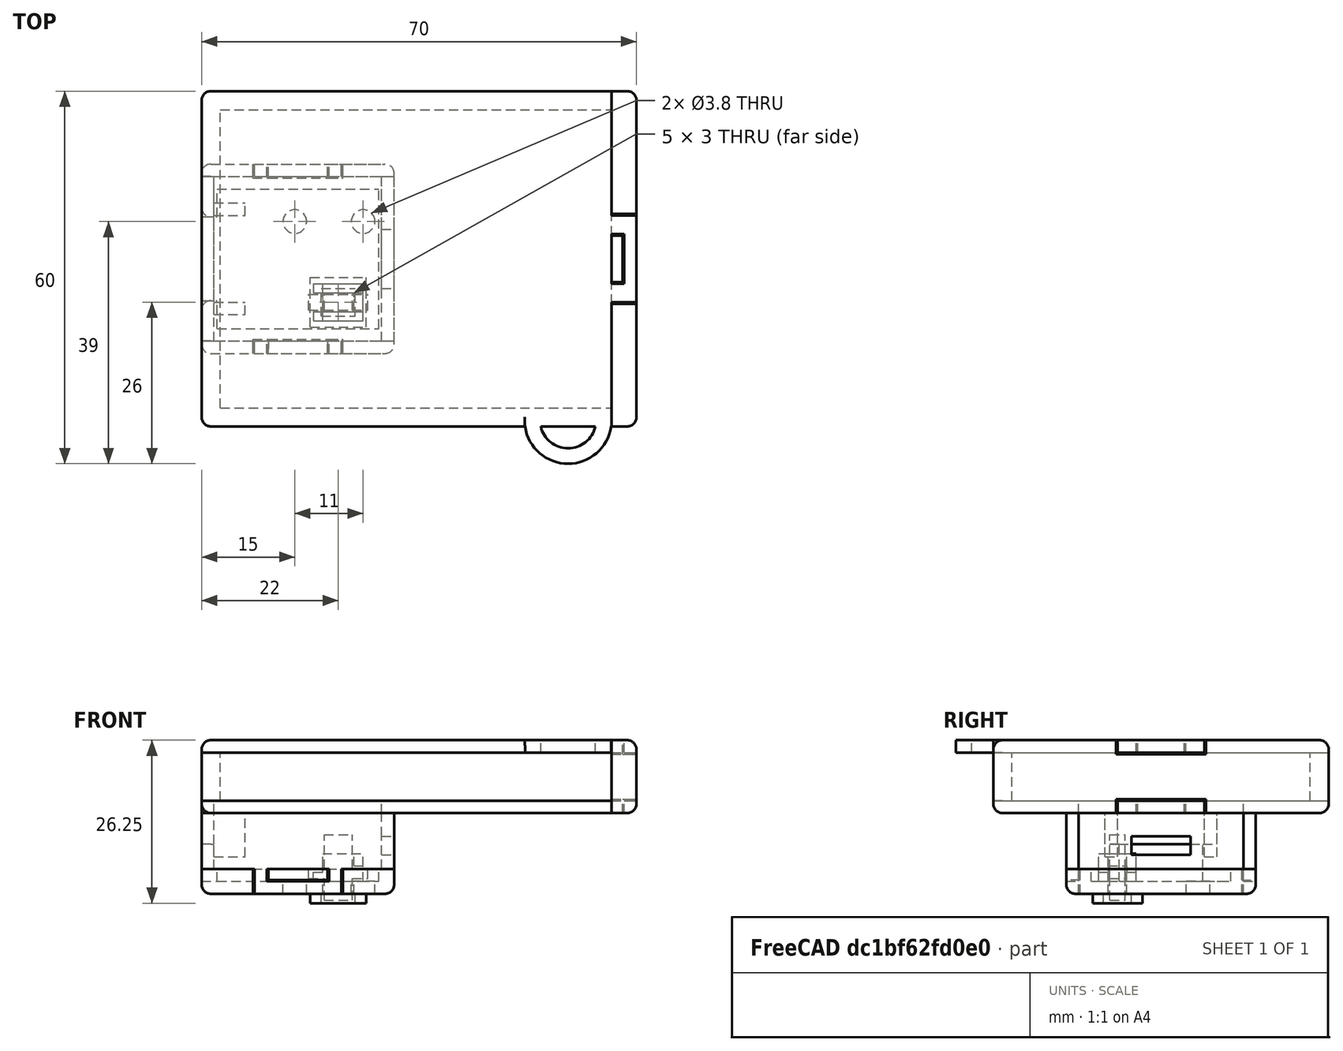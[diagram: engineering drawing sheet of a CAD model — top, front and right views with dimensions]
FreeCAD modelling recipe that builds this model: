
FCSTD DOCUMENT  (FreeCAD 0.18R16131 (Git))
Label: New_USB_Charger_Rev_1
License: All rights reserved
LicenseURL: http://en.wikipedia.org/wiki/All_rights_reserved
objects: Part::Box×62, Part::Cut×21, Part::MultiFuse×11, Part::Fillet×7, Part::Cylinder×4
note: 105 computed .brp shape members not serialized (recipe doc carries the construction recipe); baked Part::Feature solids carry a one-line shape summary decoded from their .brp

FEATURE [Part::Box] Box  label="Cube"
  AttacherType = Attacher::AttachEngine3D
  Height = 7.75
  Length = 3
  Placement = pos=(-1,-3,0) rot=(0,0,1;0rad)
  Width = 54
FEATURE [Part::Box] Box003  label="Cube003"
  AttacherType = Attacher::AttachEngine3D
  Height = 7.75
  Length = 63
  Placement = pos=(2,-3,0) rot=(0,0,1;0rad)
  Width = 3
FEATURE [Part::Box] Box004  label="Cube004"
  AttacherType = Attacher::AttachEngine3D
  Height = 7.75
  Length = 63
  Placement = pos=(2,48,0) rot=(0,0,1;0rad)
  Width = 3
FEATURE [Part::Box] Box023  label="Cube023"
  AttacherType = Attacher::AttachEngine3D
  Height = 2
  Length = 66
  Placement = pos=(-1,-3,7.75) rot=(0,0,1;0rad)
  Width = 54
FEATURE [Part::Box] Box024  label="Cube024"
  AttacherType = Attacher::AttachEngine3D
  Height = 11.75
  Length = 4
  Placement = pos=(65,-3,-2) rot=(0,0,1;0rad)
  Width = 54
FEATURE [Part::Box] Box029  label="Cube029"
  AttacherType = Attacher::AttachEngine3D
  Height = 5
  Length = 2
  Placement = pos=(-1,10.75,-7) rot=(0,0,1;0rad)
  Width = 26.5
FEATURE [Part::Box] Box031  label="Cube031"
  AttacherType = Attacher::AttachEngine3D
  Height = 4
  Length = 2
  Placement = pos=(-1,10.75,-11) rot=(0,0,1;0rad)
  Width = 6.5
FEATURE [Part::Box] Box032  label="Cube032"
  AttacherType = Attacher::AttachEngine3D
  Height = 4
  Length = 2
  Placement = pos=(-1,30.75,-11) rot=(0,0,1;0rad)
  Width = 6.5
FEATURE [Part::Box] Box033  label="Cube033"
  AttacherType = Attacher::AttachEngine3D
  Height = 3.7
  Length = 2
  Placement = pos=(28,10.75,-5.7) rot=(0,0,1;0rad)
  Width = 26.5
FEATURE [Part::Box] Box034  label="Cube034"
  AttacherType = Attacher::AttachEngine3D
  Height = 3
  Length = 2
  Placement = pos=(28,28.75,-8.7) rot=(0,0,1;0rad)
  Width = 8.5
FEATURE [Part::Box] Box035  label="Cube035"
  AttacherType = Attacher::AttachEngine3D
  Height = 3
  Length = 2
  Placement = pos=(28,10.75,-8.7) rot=(0,0,1;0rad)
  Width = 8.5
FEATURE [Part::Box] Box038  label="Cube038"
  AttacherType = Attacher::AttachEngine3D
  Height = 2.3
  Length = 2
  Placement = pos=(28,10.75,-11) rot=(0,0,1;0rad)
  Width = 26.5
FEATURE [Part::Box] Box039  label="Cube039"
  AttacherType = Attacher::AttachEngine3D
  Height = 7
  Length = 5
  Placement = pos=(1,15,-9) rot=(0,0,1;0rad)
  Width = 2
FEATURE [Part::Box] Box040  label="Cube040"
  AttacherType = Attacher::AttachEngine3D
  Height = 7
  Length = 5
  Placement = pos=(1,31,-9) rot=(0,0,1;0rad)
  Width = 2
FEATURE [Part::Box] Box041  label="Cube041"
  AttacherType = Attacher::AttachEngine3D
  Height = 2
  Length = 66
  Placement = pos=(-1,-3,-2) rot=(0,0,1;0rad)
  Width = 54
FEATURE [Part::Box] Box042  label="Cube042"
  AttacherType = Attacher::AttachEngine3D
  Height = 2
  Length = 27
  Placement = pos=(1,10.75,-2) rot=(0,0,1;0rad)
  Width = 26.5
FEATURE [Part::Box] Box043  label="Cube043"
  AttacherType = Attacher::AttachEngine3D
  Height = 2
  Length = 4
  Placement = pos=(65,17,-2) rot=(0,0,1;0rad)
  Width = 3
FEATURE [Part::Box] Box044  label="Cube044"
  AttacherType = Attacher::AttachEngine3D
  Height = 2
  Length = 4
  Placement = pos=(65,28,-2) rot=(0,0,1;0rad)
  Width = 3
FEATURE [Part::Box] Box045  label="Cube045"
  AttacherType = Attacher::AttachEngine3D
  Height = 2
  Length = 2
  Placement = pos=(67,20,-2) rot=(0,0,1;0rad)
  Width = 8
FEATURE [Part::MultiFuse] Fusion001
  Shapes = -> [Box041,Box044,Box045,Box043]
FEATURE [Part::MultiFuse] Fusion
  Shapes = -> [Box,Box003,Box004]
FEATURE [Part::Fillet] Fillet  label="Main_Sides"
  Base = -> Fusion
  Edges = 2 edges r=1.5: [Edge21,Edge28]
FEATURE [Part::Box] Box048  label="Cube048"
  AttacherType = Attacher::AttachEngine3D
  Height = 2
  Length = 4
  Placement = pos=(65,17,7.75) rot=(0,0,1;0rad)
  Width = 3
FEATURE [Part::Box] Box049  label="Cube049"
  AttacherType = Attacher::AttachEngine3D
  Height = 2
  Length = 4
  Placement = pos=(65,28,7.75) rot=(0,0,1;0rad)
  Width = 3
FEATURE [Part::Box] Box050  label="Cube050"
  AttacherType = Attacher::AttachEngine3D
  Height = 2
  Length = 2
  Placement = pos=(67,20,7.75) rot=(0,0,1;0rad)
  Width = 8
FEATURE [Part::Cylinder] Cylinder005
  Angle = 360
  AttacherType = Attacher::AttachEngine3D
  Height = 2
  Placement = pos=(58,-2,7.75) rot=(0,0,1;0rad)
  Radius = 7
FEATURE [Part::Cylinder] Cylinder006
  Angle = 360
  AttacherType = Attacher::AttachEngine3D
  Height = 2
  Placement = pos=(58,-2,7.75) rot=(0,0,1;0rad)
  Radius = 4.5
FEATURE [Part::Box] Box051  label="Cube051"
  AttacherType = Attacher::AttachEngine3D
  Height = 2
  Length = 14
  Placement = pos=(51,-3,7.75) rot=(0,0,1;0rad)
  Width = 8
FEATURE [Part::Fillet] Fillet011
  Base = -> Box024
  Edges = 8 edges r=1.5: [Edge5,Edge6,Edge7,Edge8,Edge9,Edge10,Edge11,Edge12]
FEATURE [Part::Box] Box052  label="Cube052"
  AttacherType = Attacher::AttachEngine3D
  Height = 2.25
  Length = 4
  Placement = pos=(65,16.75,7.5) rot=(0,0,1;0rad)
  Width = 3.5
FEATURE [Part::Box] Box053  label="Cube053"
  AttacherType = Attacher::AttachEngine3D
  Height = 2.25
  Length = 4
  Placement = pos=(65,27.75,7.5) rot=(0,0,1;0rad)
  Width = 3.5
FEATURE [Part::Box] Box054  label="Cube054"
  AttacherType = Attacher::AttachEngine3D
  Height = 2.25
  Length = 2.25
  Placement = pos=(66.75,20.25,7.5) rot=(0,0,1;0rad)
  Width = 7.5
FEATURE [Part::Box] Box055  label="Cube055"
  AttacherType = Attacher::AttachEngine3D
  Height = 2.25
  Length = 4
  Placement = pos=(65,16.75,-2) rot=(0,0,1;0rad)
  Width = 3.5
FEATURE [Part::Box] Box056  label="Cube056"
  AttacherType = Attacher::AttachEngine3D
  Height = 2.25
  Length = 2.25
  Placement = pos=(66.75,20.25,-2) rot=(0,0,1;0rad)
  Width = 7.5
FEATURE [Part::Box] Box057  label="Cube057"
  AttacherType = Attacher::AttachEngine3D
  Height = 2.25
  Length = 4
  Placement = pos=(65,27.75,-2) rot=(0,0,1;0rad)
  Width = 3.5
FEATURE [Part::Cut] Cut007
  Base = -> Fillet011
  Tool = -> Box057
FEATURE [Part::Cut] Cut008
  Base = -> Cut007
  Tool = -> Box055
FEATURE [Part::Cut] Cut009
  Base = -> Cut008
  Tool = -> Box056
FEATURE [Part::Cut] Cut010
  Base = -> Cut009
  Tool = -> Box053
FEATURE [Part::Cut] Cut011
  Base = -> Cut010
  Tool = -> Box052
FEATURE [Part::Cut] Cut012  label="Battery_Cover"
  Base = -> Cut011
  Tool = -> Box054
FEATURE [Part::Cut] Cut
  Base = -> Fusion001
  Tool = -> Box042
FEATURE [Part::Box] Box058  label="Cube058"
  AttacherType = Attacher::AttachEngine3D
  Height = 2
  Length = 31
  Placement = pos=(-1,8.75,-15) rot=(0,0,1;0rad)
  Width = 30.5
FEATURE [Part::Cylinder] Cylinder007
  Angle = 360
  AttacherType = Attacher::AttachEngine3D
  Height = 2
  Placement = pos=(14,30,-15) rot=(0,0,1;0rad)
  Radius = 1.9
FEATURE [Part::Cylinder] Cylinder008
  Angle = 360
  AttacherType = Attacher::AttachEngine3D
  Height = 2
  Placement = pos=(25,30,-15) rot=(0,0,1;0rad)
  Radius = 1.9
FEATURE [Part::Cut] Cut016
  Base = -> Cylinder005
  Tool = -> Cylinder006
FEATURE [Part::Cut] Cut017
  Base = -> Cut016
  Tool = -> Box051
FEATURE [Part::MultiFuse] Fusion007
  Shapes = -> [Cut017,Box023,Box048,Box050,Box049]
FEATURE [Part::Fillet] Fillet015  label="Main_Bottom"
  Base = -> Fusion007
  Edges = 8 edges r=1.5: [Edge23,Edge28,Edge29,Edge30,Edge32,Edge34,Edge55,Edge65]
FEATURE [Part::Box] Box067  label="Cube067"
  AttacherType = Attacher::AttachEngine3D
  Height = 10.5
  Length = 4.5
  Placement = pos=(18.75,15.75,-16) rot=(0,0,1;0rad)
  Width = 2.5
FEATURE [Part::Box] Box068  label="Cube068"
  AttacherType = Attacher::AttachEngine3D
  Height = 2
  Length = 5
  Placement = pos=(18.5,15.5,-15) rot=(0,0,1;0rad)
  Width = 3
FEATURE [Part::Box] Box069  label="Cube069"
  AttacherType = Attacher::AttachEngine3D
  Height = 2
  Length = 8
  Placement = pos=(17,14,-10.5) rot=(0,0,1;0rad)
  Width = 6
FEATURE [Part::Box] Box070  label="Cube070"
  AttacherType = Attacher::AttachEngine3D
  Height = 2
  Length = 5
  Placement = pos=(18.5,15.5,-10.5) rot=(0,0,1;0rad)
  Width = 3
FEATURE [Part::Box] Box071  label="Cube071"
  AttacherType = Attacher::AttachEngine3D
  Height = 9
  Length = 31
  Placement = pos=(-1,37.25,-11) rot=(0,0,1;0rad)
  Width = 2
FEATURE [Part::Box] Box072  label="Cube072"
  AttacherType = Attacher::AttachEngine3D
  Height = 4
  Length = 2
  Placement = pos=(7.5,37.25,-15) rot=(0,0,1;0rad)
  Width = 2
FEATURE [Part::Box] Box073  label="Cube073"
  AttacherType = Attacher::AttachEngine3D
  Height = 4
  Length = 2
  Placement = pos=(19.5,37.25,-15) rot=(0,0,1;0rad)
  Width = 2
FEATURE [Part::Box] Box074  label="Cube074"
  AttacherType = Attacher::AttachEngine3D
  Height = 2
  Length = 10
  Placement = pos=(9.5,37.25,-15) rot=(0,0,1;0rad)
  Width = 2
FEATURE [Part::Box] Box075  label="Cube075"
  AttacherType = Attacher::AttachEngine3D
  Height = 9
  Length = 31
  Placement = pos=(-1,8.75,-11) rot=(0,0,1;0rad)
  Width = 2
FEATURE [Part::Box] Box076  label="Cube076"
  AttacherType = Attacher::AttachEngine3D
  Height = 4
  Length = 2
  Placement = pos=(7.5,8.75,-15) rot=(0,0,1;0rad)
  Width = 2
FEATURE [Part::Box] Box077  label="Cube077"
  AttacherType = Attacher::AttachEngine3D
  Height = 4
  Length = 2
  Placement = pos=(19.5,8.75,-15) rot=(0,0,1;0rad)
  Width = 2
FEATURE [Part::Box] Box078  label="Cube078"
  AttacherType = Attacher::AttachEngine3D
  Height = 2
  Length = 10
  Placement = pos=(9.5,8.75,-15) rot=(0,0,1;0rad)
  Width = 2
FEATURE [Part::Box] Box079  label="Cube079"
  AttacherType = Attacher::AttachEngine3D
  Height = 2
  Length = 31
  Placement = pos=(-1,8.75,-13) rot=(0,0,1;0rad)
  Width = 2
FEATURE [Part::Box] Box080  label="Cube080"
  AttacherType = Attacher::AttachEngine3D
  Height = 2
  Length = 26
  Placement = pos=(1.5,10.75,-13) rot=(0,0,1;0rad)
  Width = 2
FEATURE [Part::Box] Box081  label="Cube081"
  AttacherType = Attacher::AttachEngine3D
  Height = 2
  Length = 31
  Placement = pos=(-1,37.25,-13) rot=(0,0,1;0rad)
  Width = 2
FEATURE [Part::Box] Box082  label="Cube082"
  AttacherType = Attacher::AttachEngine3D
  Height = 2
  Length = 26
  Placement = pos=(1.5,35.25,-13) rot=(0,0,1;0rad)
  Width = 2
FEATURE [Part::MultiFuse] Fusion012
  Shapes = -> [Box080,Box079,Box081,Box082,Box058]
FEATURE [Part::Fillet] Fillet019
  Base = -> Fusion012
  Edges = 12 edges r=1.5: [Edge1,Edge2,Edge3,Edge4,Edge5,Edge7,Edge10,Edge12,Edge17,Edge32,Edge33,Edge35]
FEATURE [Part::Box] Box083  label="Cube083"
  AttacherType = Attacher::AttachEngine3D
  Height = 4
  Length = 2.5
  Placement = pos=(19.25,8.75,-15) rot=(0,0,1;0rad)
  Width = 2.25
FEATURE [Part::Box] Box084  label="Cube084"
  AttacherType = Attacher::AttachEngine3D
  Height = 4
  Length = 2.5
  Placement = pos=(7.25,8.75,-15) rot=(0,0,1;0rad)
  Width = 2.25
FEATURE [Part::Box] Box085  label="Cube085"
  AttacherType = Attacher::AttachEngine3D
  Height = 2.25
  Length = 10
  Placement = pos=(9.5,8.75,-15) rot=(0,0,1;0rad)
  Width = 2.25
FEATURE [Part::Box] Box086  label="Cube086"
  AttacherType = Attacher::AttachEngine3D
  Height = 4
  Length = 2.5
  Placement = pos=(7.25,37,-15) rot=(0,0,1;0rad)
  Width = 2.25
FEATURE [Part::Box] Box087  label="Cube087"
  AttacherType = Attacher::AttachEngine3D
  Height = 4
  Length = 2.5
  Placement = pos=(19.25,37,-15) rot=(0,0,1;0rad)
  Width = 2.25
FEATURE [Part::Box] Box088  label="Cube088"
  AttacherType = Attacher::AttachEngine3D
  Height = 2.25
  Length = 10
  Placement = pos=(9.5,37,-15) rot=(0,0,1;0rad)
  Width = 2.25
FEATURE [Part::MultiFuse] Fusion015
  Shapes = -> [Cut,Box029,Box031,Box032,Box033,Box034,Box035,Box038,Box039,Box040]
FEATURE [Part::Cut] Cut022
  Base = -> Fillet019
  Tool = -> Box084
FEATURE [Part::Cut] Cut023
  Base = -> Cut022
  Tool = -> Box083
FEATURE [Part::Cut] Cut024
  Base = -> Cut023
  Tool = -> Box085
FEATURE [Part::MultiFuse] Fusion016
  Shapes = -> [Box078,Box077,Box076,Box075]
FEATURE [Part::Fillet] Fillet023  label="Top_Side_1"
  Base = -> Fusion016
  Edges = 5 edges r=1.5: [Edge1,Edge9,Edge21,Edge28,Edge43]
FEATURE [Part::Cut] Cut025
  Base = -> Cut024
  Tool = -> Box088
FEATURE [Part::Cut] Cut026
  Base = -> Cut025
  Tool = -> Box087
FEATURE [Part::Cut] Cut027
  Base = -> Cut026
  Tool = -> Box086
FEATURE [Part::MultiFuse] Fusion017
  Shapes = -> [Box071,Box074,Box073,Box072]
FEATURE [Part::Fillet] Fillet024  label="Top_Side_2"
  Base = -> Fusion017
  Edges = 5 edges r=1.5: [Edge7,Edge25,Edge41,Edge44,Edge46]
FEATURE [Part::Box] Box089  label="Cube089"
  AttacherType = Attacher::AttachEngine3D
  Height = 2
  Length = 2.5
  Placement = pos=(27.5,10.75,-13) rot=(0,0,1;0rad)
  Width = 26.5
FEATURE [Part::Box] Box090  label="Cube090"
  AttacherType = Attacher::AttachEngine3D
  Height = 2
  Length = 2.5
  Placement = pos=(-1,10.75,-13) rot=(0,0,1;0rad)
  Width = 6.5
FEATURE [Part::Box] Box091  label="Cube091"
  AttacherType = Attacher::AttachEngine3D
  Height = 2
  Length = 2.5
  Placement = pos=(-1,30.75,-13) rot=(0,0,1;0rad)
  Width = 6.5
FEATURE [Part::Fillet] Fillet025  label="Main_Top"
  Base = -> Fusion015
  Edges = 11 edges r=1.5: [Edge36,Edge79,Edge84,Edge89,Edge90,Edge96,Edge98,Edge99,Edge126,Edge129,Edge155]
FEATURE [Part::Cut] Cut028
  Base = -> Cut027
  Tool = -> Box068
FEATURE [Part::Cut] Cut029
  Base = -> Cut028
  Tool = -> Cylinder007
FEATURE [Part::Cut] Cut030
  Base = -> Cut029
  Tool = -> Cylinder008
FEATURE [Part::MultiFuse] Fusion018  label="Top_Cover1"
  Shapes = -> [Box091,Box090,Box089,Cut030]
FEATURE [Part::Box] Box092  label="Cube092"
  AttacherType = Attacher::AttachEngine3D
  Height = 1.5
  Length = 2.5
  Placement = pos=(16.25,15.75,-12.5) rot=(0,0,1;0rad)
  Width = 2.5
FEATURE [Part::Box] Box093  label="Cube093"
  AttacherType = Attacher::AttachEngine3D
  Height = 1.5
  Length = 2.5
  Placement = pos=(23.25,15.75,-12.5) rot=(0,0,1;0rad)
  Width = 2.5
FEATURE [Part::Box] Box094  label="Cube094"
  AttacherType = Attacher::AttachEngine3D
  Height = 2.5
  Length = 8
  Placement = pos=(17,18.5,-13) rot=(0,0,1;0rad)
  Width = 1.5
FEATURE [Part::Box] Box095  label="Cube095"
  AttacherType = Attacher::AttachEngine3D
  Height = 2.5
  Length = 8
  Placement = pos=(17,14,-13) rot=(0,0,1;0rad)
  Width = 1.5
FEATURE [Part::Box] Box096  label="Cube096"
  AttacherType = Attacher::AttachEngine3D
  Height = 1.5
  Length = 9
  Placement = pos=(16.5,13,-16.5) rot=(0,0,1;0rad)
  Width = 8
FEATURE [Part::Box] Box097  label="Cube097"
  AttacherType = Attacher::AttachEngine3D
  Height = 1.5
  Length = 5.5
  Placement = pos=(18.25,14.75,-16.5) rot=(0,0,1;0rad)
  Width = 4.5
FEATURE [Part::Cut] Cut032  label="Button_Guard"
  Base = -> Box096
  Tool = -> Box097
FEATURE [Part::MultiFuse] Fusion022
  Shapes = -> [Box094,Box095,Box069]
FEATURE [Part::Cut] Cut033  label="Button_Guide1"
  Base = -> Fusion022
  Tool = -> Box070
FEATURE [Part::MultiFuse] Fusion023  label="Top_Cover"
  Shapes = -> [Fusion018,Cut032]
FEATURE [Part::MultiFuse] Fusion024  label="Button"
  Shapes = -> [Box092,Box093,Box067]
FEATURE [Part::Box] Box098  label="Cube098"
  AttacherType = Attacher::AttachEngine3D
  Height = 3
  Length = 2
  Placement = pos=(16.5,14,-11.5) rot=(0,0,1;0rad)
  Width = 6
FEATURE [Part::Cut] Cut034  label="Button_guide"
  Base = -> Cut033
  Tool = -> Box098
